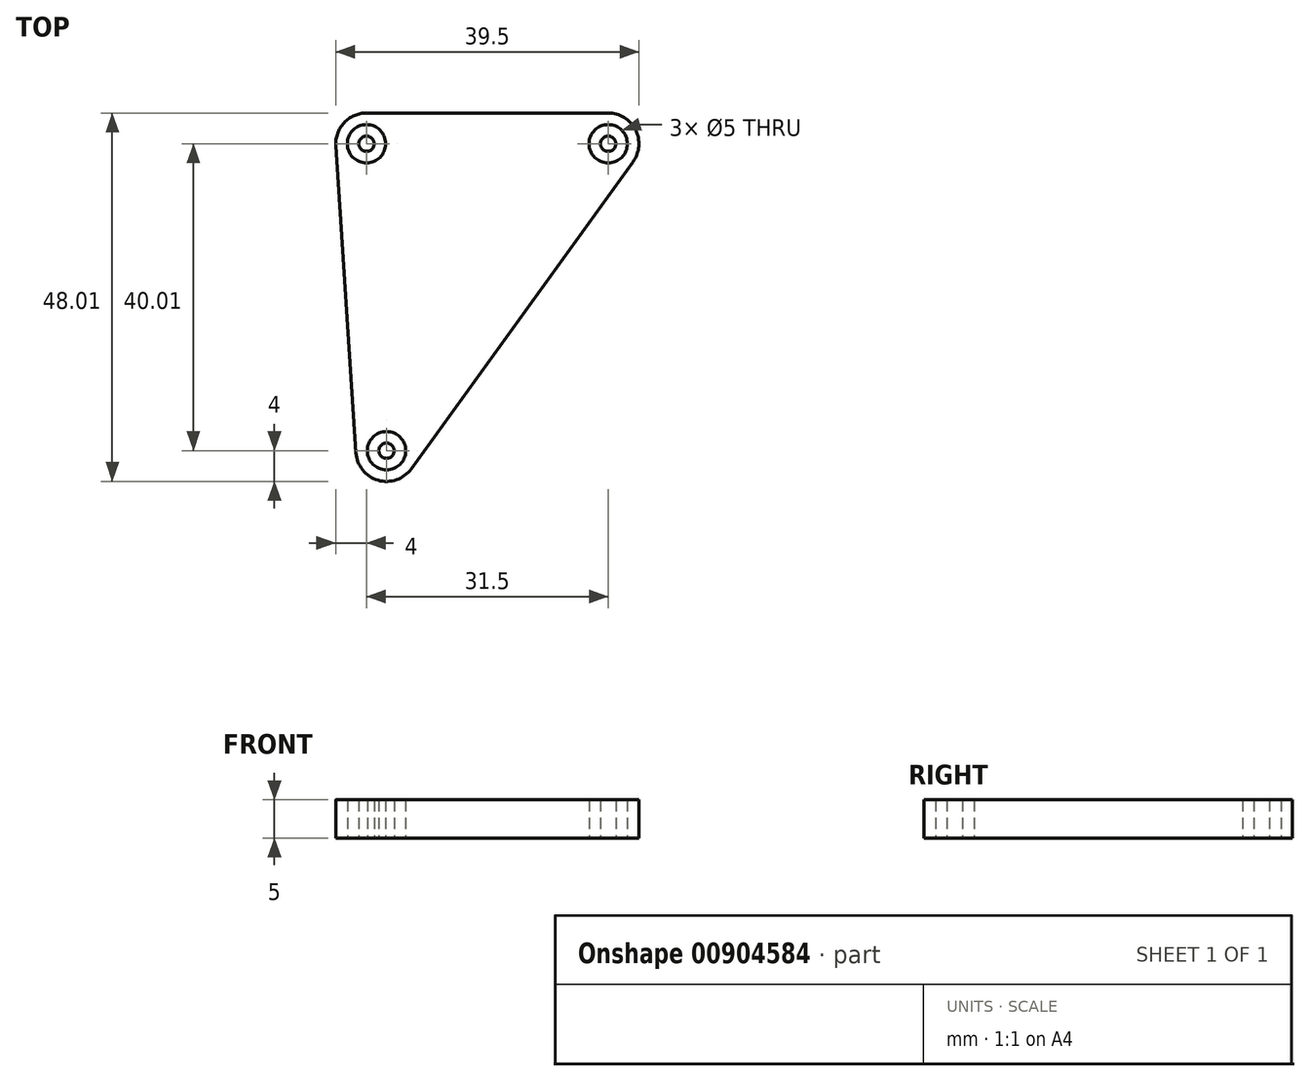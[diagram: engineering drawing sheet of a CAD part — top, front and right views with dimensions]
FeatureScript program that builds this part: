
annotation { "Feature Type Name" : "Feature", "Feature Type Description" : "" }
export const myFeature = defineFeature(function(context is Context, id is Id, definition is map)
    precondition{}
    {
        {
            var Q0;
            Q0=qCreatedBy(makeId("Top.planeOp"),FACE);
            var sketch = newSketch(context, id + "F0", { "sketchPlane" : qUnion([Q0])});
            skArc(sketch, "E0", {"start": v(-7.1, -37.53) * mm, "mid": v(-4.2, -41.11) * mm, "end": v(0.14, -39.61) * mm});
            skArc(sketch, "E1", {"start": v(-5.7, 6.74) * mm, "mid": v(-8.63, 5.47) * mm, "end": v(-9.7, 2.48) * mm});
            skArc(sketch, "E2", {"start": v(29.03, 0.4) * mm, "mid": v(29.35, 4.56) * mm, "end": v(25.79, 6.74) * mm});
            skLineSegment(sketch, "E3", {"start": v(-9.7, 2.48) * mm, "end": v(-7.1, -37.53) * mm});
            skLineSegment(sketch, "E4", {"start": v(-5.7, 6.74) * mm, "end": v(25.79, 6.74) * mm});
            skCircle(sketch, "E5", {"center": v(-5.7, 2.74) * mm, "radius": 2.5 * mm});
            skCircle(sketch, "E6", {"center": v(-5.7, 2.74) * mm, "radius": 1 * mm});
            skCircle(sketch, "E7", {"center": v(25.79, 2.74) * mm, "radius": 2.5 * mm});
            skCircle(sketch, "E8", {"center": v(25.79, 2.74) * mm, "radius": 1 * mm});
            skCircle(sketch, "E9", {"center": v(-3.1, -37.27) * mm, "radius": 2.5 * mm});
            skCircle(sketch, "E10", {"center": v(-3.1, -37.27) * mm, "radius": 1 * mm});
            skLineSegment(sketch, "E11", {"start": v(0.14, -39.61) * mm, "end": v(29.03, 0.4) * mm});
            skSolve(sketch);
        }
        {
            var Q0;
            Q0=makeQuery(id+"F0.imprint","IMPRINT",FACE,{"disambiguationData":[TD([[makeQuery(id+"F0.imprint","IMPRINT",EDGE,{"derivedFrom":sQuery(id+"F0.wireOp",EDGE,"E0")}),1.0]])]});
            var Q1;
            Q1=makeQuery(id+"F0.imprint","IMPRINT",FACE,{"disambiguationData":[TD([[makeQuery(id+"F0.imprint","IMPRINT",EDGE,{"derivedFrom":sQuery(id+"F0.wireOp",EDGE,"E6")}),1.0]])]});
            var Q2;
            Q2=makeQuery(id+"F0.imprint","IMPRINT",FACE,{"disambiguationData":[TD([[makeQuery(id+"F0.imprint","IMPRINT",EDGE,{"derivedFrom":sQuery(id+"F0.wireOp",EDGE,"E10")}),1.0]])]});
            var Q3;
            Q3=makeQuery(id+"F0.imprint","IMPRINT",FACE,{"disambiguationData":[TD([[makeQuery(id+"F0.imprint","IMPRINT",EDGE,{"derivedFrom":sQuery(id+"F0.wireOp",EDGE,"E8")}),1.0]])]});
            extrude(context, id + "F1", {"entities" : qUnion([Q0, Q1, Q2, Q3]), "endBound" : BoundingType.SYMMETRIC, "depth" : 5 * mm, "offsetDistance" : 25.4 * mm});
        }
    });
